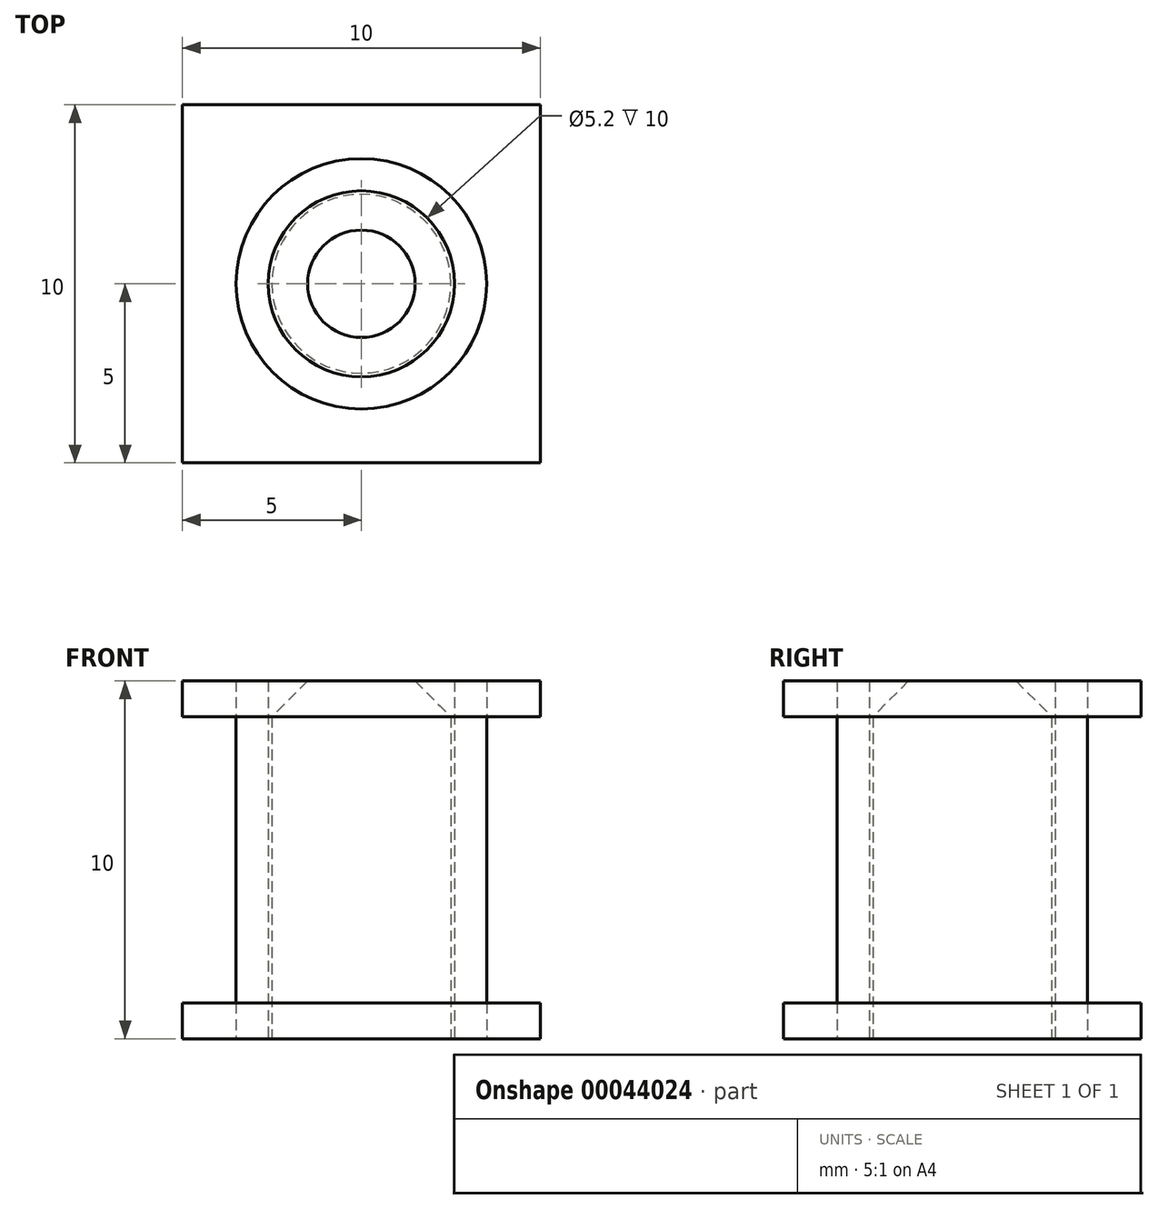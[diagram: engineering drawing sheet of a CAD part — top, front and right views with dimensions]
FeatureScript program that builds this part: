
annotation { "Feature Type Name" : "Feature", "Feature Type Description" : "" }
export const myFeature = defineFeature(function(context is Context, id is Id, definition is map)
    precondition{}
    {
        {
            var Q0;
            Q0=qCreatedBy(makeId("Top.planeOp"),FACE);
            var sketch = newSketch(context, id + "F0", { "sketchPlane" : qUnion([Q0])});
            skCircle(sketch, "E0", {"center": v(0, 0) * mm, "radius": 2.5 * mm});
            skCircle(sketch, "E1", {"center": v(0, 0) * mm, "radius": 3.5 * mm});
            skCircle(sketch, "E2", {"center": v(0, 0) * mm, "radius": 2.6 * mm});
            skSolve(sketch);
        }
        {
            var Q0;
            Q0=makeQuery(id+"F0.imprint","IMPRINT",FACE,{"disambiguationData":[TD([[makeQuery(id+"F0.imprint","IMPRINT",EDGE,{"derivedFrom":sQuery(id+"F0.wireOp",EDGE,"E0")}),1.0]])]});
            extrude(context, id + "F1", {"entities" : qUnion([Q0]), "endBound" : BoundingType.SYMMETRIC, "depth" : 10 * mm});
        }
        {
            var Q0;
            Q0=makeQuery(id+"F0.imprint","IMPRINT",FACE,{"disambiguationData":[TD([[makeQuery(id+"F0.imprint","IMPRINT",EDGE,{"derivedFrom":sQuery(id+"F0.wireOp",EDGE,"E1")}),1.0]])]});
            extrude(context, id + "F2", {"entities" : qUnion([Q0]), "endBound" : BoundingType.SYMMETRIC, "depth" : 10 * mm});
        }
        {
            var Q0;
            Q0=makeQuery(id+"F1.opExtrude","CAP_EDGE",EDGE,{"disambiguationData":[OSD([sQuery(id+"F0.wireOp",EDGE,"E0")])],"isStart":false});
            chamfer(context, id + "F3", {"entities" : qUnion([Q0]), "width" : 1 * mm, "tangentPropagation" : true});
        }
        {
            var Q0;
            Q0=qCreatedBy(makeId("Top.planeOp"),FACE);
            var sketch = newSketch(context, id + "F4", { "sketchPlane" : qUnion([Q0])});
            skLineSegment(sketch, "E3.rect.bottom", {"start": v(-5, 5) * mm, "end": v(5, 5) * mm});
            skLineSegment(sketch, "E3.rect.top", {"start": v(-5, -5) * mm, "end": v(5, -5) * mm});
            skLineSegment(sketch, "E3.rect.left", {"start": v(-5, 5) * mm, "end": v(-5, -5) * mm});
            skLineSegment(sketch, "E3.rect.right", {"start": v(5, 5) * mm, "end": v(5, -5) * mm});
            skPoint(sketch, "E3.rect.middle", {"position": v(0, 0) * mm});
            skSolve(sketch);
        }
        {
            var Q0;
            Q0=makeQuery(id+"F4.imprint","IMPRINT",FACE,{"disambiguationData":[TD([[makeQuery(id+"F4.imprint","IMPRINT",EDGE,{"derivedFrom":sQuery(id+"F4.wireOp",EDGE,"E3.rect.bottom")}),-1.0]])]});
            extrude(context, id + "F5", {"entities" : qUnion([Q0]), "depth" : 1 * mm});
        }
        {
            var Q0;
            Q0=makeQuery(id+"F5.opExtrude","SWEPT_BODY",BODY,{"disambiguationData":[OSD([sQuery(id+"F4.wireOp",EDGE,"E3.rect.bottom"),sQuery(id+"F4.wireOp",EDGE,"E3.rect.top"),sQuery(id+"F4.wireOp",EDGE,"E3.rect.left"),sQuery(id+"F4.wireOp",EDGE,"E3.rect.right")])]});
            var Q1;
            Q1=makeQuery(id+"F2.opExtrude","SWEPT_FACE",FACE,{"disambiguationData":[OSD([sQuery(id+"F0.wireOp",EDGE,"E1")])]});
            transform(context, id + "F6", {"entities" : qUnion([Q0]), "transformType" : TransformType.TRANSLATION_DISTANCE, "transformDirection" : qUnion([Q1]), "distance" : 5 * mm, "makeCopy" : true});
        }
        {
            var Q0;
            Q0=makeQuery(id+"F5.opExtrude","SWEPT_BODY",BODY,{"disambiguationData":[OSD([sQuery(id+"F4.wireOp",EDGE,"E3.rect.bottom"),sQuery(id+"F4.wireOp",EDGE,"E3.rect.top"),sQuery(id+"F4.wireOp",EDGE,"E3.rect.left"),sQuery(id+"F4.wireOp",EDGE,"E3.rect.right")])]});
            var Q1;
            Q1=makeQuery(id+"F2.opExtrude","SWEPT_FACE",FACE,{"disambiguationData":[OSD([sQuery(id+"F0.wireOp",EDGE,"E1")])]});
            transform(context, id + "F7", {"entities" : qUnion([Q0]), "transformType" : TransformType.TRANSLATION_DISTANCE, "transformDirection" : qUnion([Q1]), "distance" : 4 * mm, "oppositeDirection" : true, "makeCopy" : false});
        }
    });
